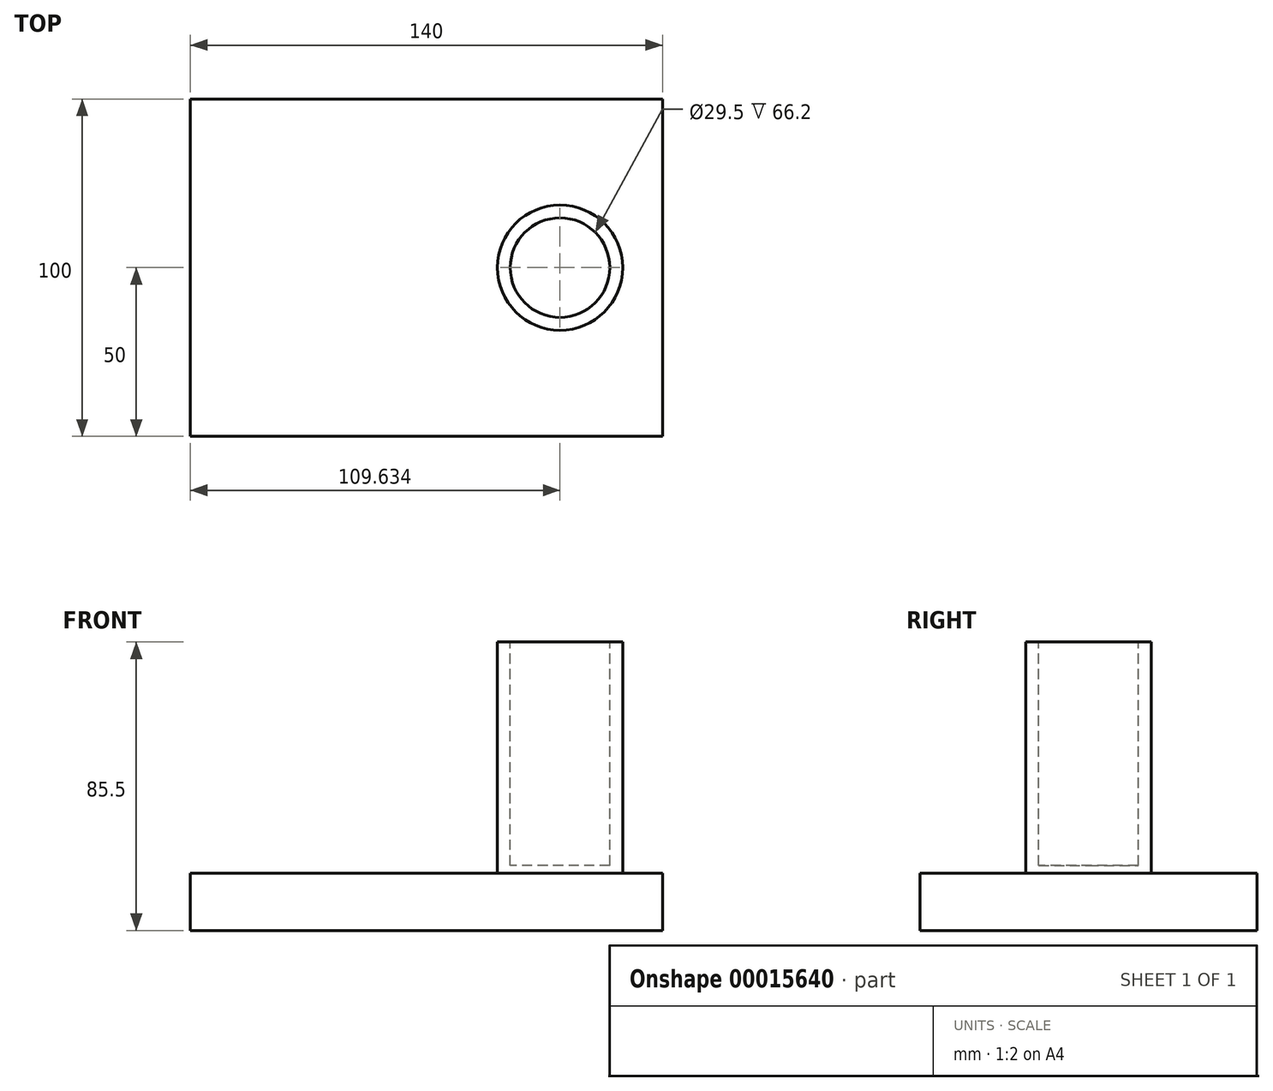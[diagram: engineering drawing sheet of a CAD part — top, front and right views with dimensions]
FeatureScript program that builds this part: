
annotation { "Feature Type Name" : "Feature", "Feature Type Description" : "" }
export const myFeature = defineFeature(function(context is Context, id is Id, definition is map)
    precondition{}
    {
        {
            var Q0;
            Q0=qCreatedBy(makeId("Top.planeOp"),FACE);
            var sketch = newSketch(context, id + "F0", { "sketchPlane" : qUnion([Q0])});
            skLineSegment(sketch, "E0.rect.bottom", {"start": v(-62.5, -50) * mm, "end": v(62.5, -50) * mm});
            skLineSegment(sketch, "E0.rect.top", {"start": v(-62.5, 50) * mm, "end": v(62.5, 50) * mm});
            skLineSegment(sketch, "E0.rect.left", {"start": v(-62.5, -50) * mm, "end": v(-62.5, 50) * mm});
            skLineSegment(sketch, "E0.rect.right", {"start": v(62.5, -50) * mm, "end": v(62.5, 50) * mm});
            skPoint(sketch, "E0.rect.middle", {"position": v(0, 0) * mm});
            skSolve(sketch);
        }
        {
            var Q0;
            Q0=makeQuery(id+"F0.imprint","IMPRINT",FACE,{"disambiguationData":[TD([[makeQuery(id+"F0.imprint","IMPRINT",EDGE,{"derivedFrom":sQuery(id+"F0.wireOp",EDGE,"E0.rect.bottom")}),1.0]])]});
            var sketch = newSketch(context, id + "F1", { "sketchPlane" : qUnion([Q0])});
            skCircle(sketch, "E1", {"center": v(32.13, 0) * mm, "radius": 18.58 * mm});
            skSolve(sketch);
        }
        {
            var Q0;
            Q0=makeQuery(id+"F1.imprint","IMPRINT",FACE,{"disambiguationData":[TD([[makeQuery(id+"F1.imprint","IMPRINT",EDGE,{"derivedFrom":sQuery(id+"F1.wireOp",EDGE,"E1")}),1.0]])]});
            extrude(context, id + "F2", {"entities" : qUnion([Q0]), "depth" : 86.3 * mm});
        }
        {
            var Q0;
            Q0=makeQuery(id+"F0.imprint","IMPRINT",FACE,{"disambiguationData":[TD([[makeQuery(id+"F0.imprint","IMPRINT",EDGE,{"derivedFrom":sQuery(id+"F0.wireOp",EDGE,"E0.rect.bottom")}),1.0]])]});
            extrude(context, id + "F3", {"entities" : qUnion([Q0]), "operationType" : NewBodyOperationType.ADD, "depth" : 17 * mm});
        }
        {
            var Q0;
            Q0=makeQuery(id+"F2.opExtrude","CAP_FACE",FACE,{"disambiguationData":[OSD([sQuery(id+"F1.wireOp",EDGE,"E1")])],"isStart":false});
            var sketch = newSketch(context, id + "F4", { "sketchPlane" : qUnion([Q0])});
            skCircle(sketch, "E2", {"center": v(32.13, 0) * mm, "radius": 14.75 * mm});
            skSolve(sketch);
        }
        {
            var Q0;
            Q0=makeQuery(id+"F4.imprint","IMPRINT",FACE,{"disambiguationData":[TD([[makeQuery(id+"F4.imprint","IMPRINT",EDGE,{"derivedFrom":sQuery(id+"F4.wireOp",EDGE,"E2")}),1.0]])]});
            extrude(context, id + "F5", {"entities" : qUnion([Q0]), "operationType" : NewBodyOperationType.REMOVE, "oppositeDirection" : true, "depth" : 67 * mm});
        }
        {
            var Q0;
            Q0=makeQuery(id+"F2.opExtrude","CAP_FACE",FACE,{"disambiguationData":[OSD([sQuery(id+"F1.wireOp",EDGE,"E1")])],"isStart":false});
            extrude(context, id + "F6", {"entities" : qUnion([Q0]), "operationType" : NewBodyOperationType.REMOVE, "oppositeDirection" : true, "depth" : 0.8 * mm});
        }
        {
            var Q0;
            Q0=makeQuery(id+"F3.opExtrude","SWEPT_FACE",FACE,{"disambiguationData":[OSD([sQuery(id+"F0.wireOp",EDGE,"E0.rect.left")])]});
            extrude(context, id + "F7", {"entities" : qUnion([Q0]), "operationType" : NewBodyOperationType.ADD, "depth" : 15 * mm});
        }
    });
